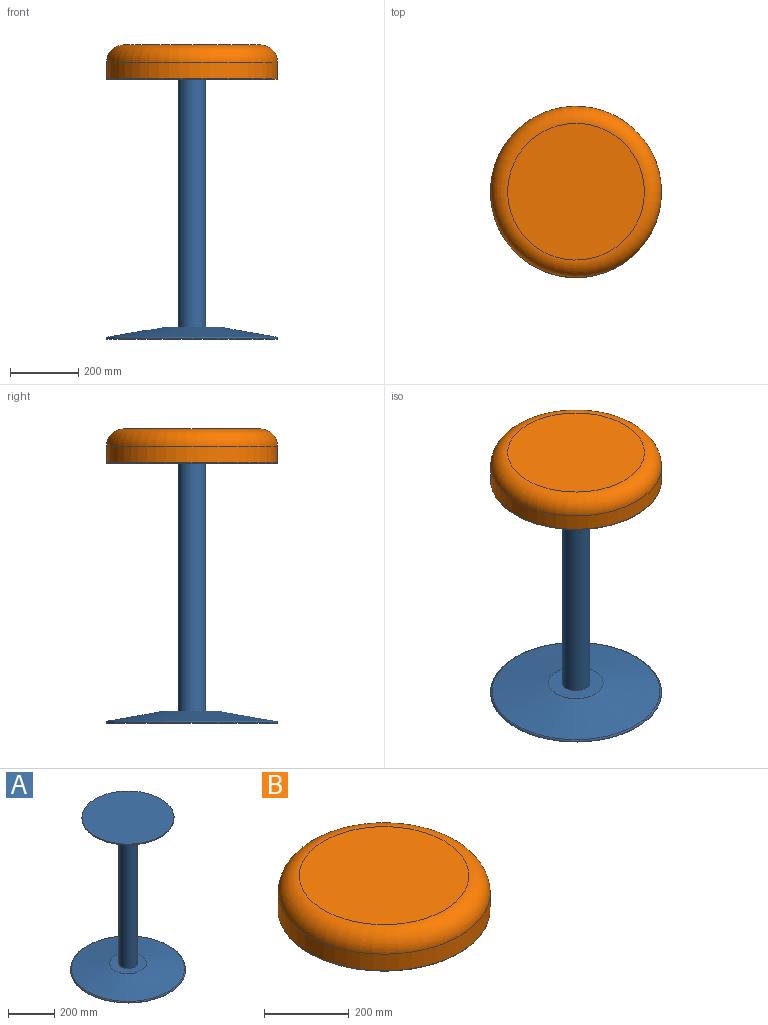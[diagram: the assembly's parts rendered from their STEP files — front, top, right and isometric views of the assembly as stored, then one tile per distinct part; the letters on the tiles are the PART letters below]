
ASSEMBLY  parts=2 mates=1
PART A: 9 faces, bbox 541.2x541.2x812.7 mm
  f0: cylinder r=40mm len=770mm, axis (0,0,-1), area 193522.1mm2, adj f2,f8
  f1: cone r=250mm half-angle=80deg, axis (0,0,-1), area 172497mm2, adj f2,f5
  f2: plane 159.72x159.72mm, normal (0,0,1), area 15010.1mm2, adj f0,f1
  f3: cylinder r=250mm len=500mm, axis (0,0,1), area 1263.7mm2, adj f4,f5
  f4: plane 500x500mm, normal (0,0,-1), area 196349.5mm2, adj f3
  f5: torus R=245mm, axis (0,0,-1), area 10901.6mm2, adj f1,f3
  f6: plane 400x400mm, normal (0,0,1), area 125663.7mm2, adj f7
  f7: cylinder r=200mm len=400mm, axis (0,0,-1), area 6283.2mm2, adj f6,f8
  f8: plane 400x400mm, normal (0,0,-1), area 120637.2mm2, adj f0,f7
PART B: 8 faces, bbox 541.2x541.2x100 mm
  f0: cylinder r=250mm len=500mm, axis (0,0,-1), area 75398.2mm2, adj f5,f6
  f1: plane 400x400mm, normal (0,0,1), area 125663.7mm2, adj f5
  f2: plane 496x496mm, normal (0,0,-1), area 9236.3mm2, adj f6,f7
  f3: cylinder r=240mm len=480mm, axis (0,0,-1), area 72382.3mm2, adj f4,f7
  f4: plane 480x480mm, normal (0,0,-1), area 180955.7mm2, adj f3
  f5: torus R=200mm, axis (0,0,1), area 114404mm2, adj f0,f1
  f6: torus R=248mm, axis (0,0,1), area 4920.5mm2, adj f0,f2
  f7: torus R=242mm, axis (0,0,1), area 4751.8mm2, adj f2,f3
PLACE A t=(-98.38,38.42,-257.16)mm
PLACE B t=(-98.38,38.42,497.84)mm
MATE fastened B.f3 <-> A.f7  axis (0,0,-1) through (-98.38,38.42,547.84)mm
